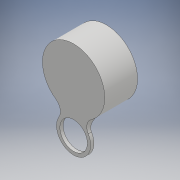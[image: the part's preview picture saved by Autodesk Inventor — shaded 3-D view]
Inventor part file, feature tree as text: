
AUTODESK INVENTOR PART (.ipt)
format: ipt  version: 2018 (Build 220112000, 112)  size: 305,664 bytes
history: native  units: mm
features: extrude x4, sketch x4, fillet x2
ambient origin geometry x8: Origin, YZ Plane, XZ Plane, XY Plane, X Axis, Y Axis, Z Axis, Center Point
bodies: Solid1 (feature_tree)
feature tree (10):
  extrude  "Extrusion1"  Depth=0.635mm TaperAngle=0.0deg
  extrude  "Extrusion2"  Depth=5.715mm TaperAngle=0.0deg
  extrude  "Extrusion3"  Depth=3.302mm
  extrude  "Extrusion4"  Depth=2.0mm TaperAngle=0.0deg
  fillet  "Fillet1"  Radius=0.635mm
  fillet  "Fillet2"  Radius=2.0mm
  sketch  "Sketch1"  dims[d0=12.065mm d1=0.635mm d2=0.0mm]
  sketch  "Sketch2"  dims[d3=10.795mm d4=5.715mm d5=0.0mm]
  sketch  "Sketch3"  dims[d6=3.302mm d7=6.604mm]
  sketch  "Sketch4"  dims[d8=5.334mm d9=0.635mm d10=0.0mm d11=0.635mm d12=0.0mm d13=2.0mm d14=2.0mm]
